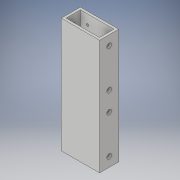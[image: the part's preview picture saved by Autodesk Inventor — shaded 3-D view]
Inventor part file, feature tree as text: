
AUTODESK INVENTOR PART (.ipt)
format: ipt  version: 2017 (Build 210142000, 142)  size: 137,728 bytes
history: native  units: in
note: dims shown in document units (in); Inventor stores cm internally (conversion verified against a paired STEP export)
features: sketch x3, hole x2, extrude x1
ambient origin geometry x8: Origin, YZ Plane, XZ Plane, XY Plane, X Axis, Y Axis, Z Axis, Center Point
bodies: Solid1 (feature_tree)
feature tree (6):
  extrude  "Extrusion1"  Depth=1.0in
  hole  "Hole2"  [1 undecoded]
  hole  "Hole3"  [1 undecoded]
  sketch  "Sketch1"  dims[d0=2.0in d1=1.0in]
  sketch  "Sketch2"  dims[d2=1.75in d3=0.75in]
  sketch  "Sketch3"  dims[d4=0.125in d5=0.125in d6=6.0in d7=0.0in d8=0.25in d9=0.5in d10=0.25in d11=0.5in d19=0.25in d20=0.75in d21=0.375in d22=0.25in d23=0.5635in d24=1.0in d25=0.8108in d27=0.5in d28=0.5in d30=0.125in d31=1.0in d32=0.125in d33=0.75in d34=0.375in d35=0.25in d36=0.5635in d37=0.125in d38=0.8108in]
note: 2 required parameter values undecoded (feature->parameter linkage not recoverable at this tier; creation-order binding heuristic only, values carry confidence <= 0.55)
